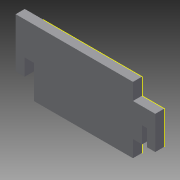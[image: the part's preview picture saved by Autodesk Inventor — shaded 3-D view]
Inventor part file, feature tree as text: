
AUTODESK INVENTOR PART (.ipt)
format: ipt  version: 2014 SP1 (Build 180222100, 222)  size: 147,968 bytes
history: native  units: mm
features: sketch x6, extrude x5
ambient origin geometry x8: Origin, YZ Plane, XZ Plane, XY Plane, X Axis, Y Axis, Z Axis, Center Point
bodies: Solid1 (feature_tree)
feature tree (11):
  extrude  "Extrusion1"  Depth=40.0mm
  extrude  "Extrusion2"  TaperAngle=0.0deg  [1 undecoded]
  extrude  "Extrusion3"  Depth=10.0mm
  sketch  "Sketch4"  dims[d6=5.5mm d7=0.0mm]
  extrude  "Extrusion4"  TaperAngle=0.0deg  [1 undecoded]
  extrude  "Extrusion5"  Depth=3.0mm
  sketch  "Sketch1"  dims[d0=60.0mm d1=40.0mm]
  sketch  "Sketch2"  dims[d2=5.5mm d3=0.0mm]
  sketch  "Sketch3"  dims[d4=13.5mm d5=10.0mm]
  sketch  "Sketch5"  dims[d8=5.5mm d9=3.0mm]
  sketch  "Sketch6"  dims[d10=10.0mm d11=5.5mm d12=0.0mm d14=11.0mm d15=10.0mm d16=5.5mm d17=0.0mm d20=0.0mm d21=5.5mm d22=5.5mm d23=0.0mm]
note: 2 required parameter values undecoded (feature->parameter linkage not recoverable at this tier; creation-order binding heuristic only, values carry confidence <= 0.55)
